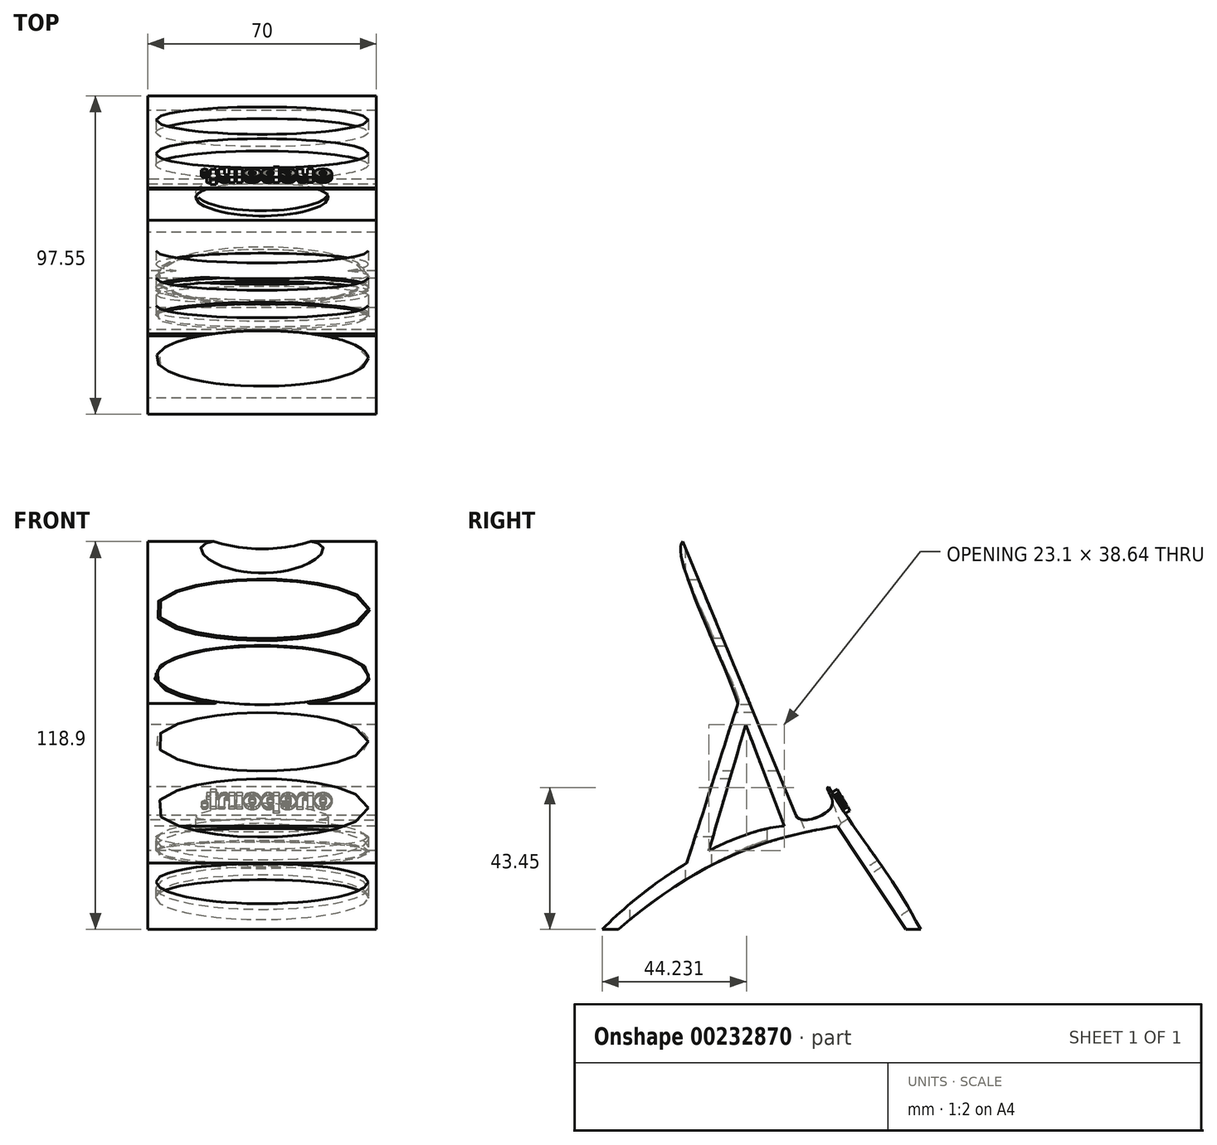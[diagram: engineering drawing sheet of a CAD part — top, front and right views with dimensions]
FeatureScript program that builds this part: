
annotation { "Feature Type Name" : "Feature", "Feature Type Description" : "" }
export const myFeature = defineFeature(function(context is Context, id is Id, definition is map)
    precondition{}
    {
        {
            var Q0;
            Q0=qCreatedBy(makeId("Right.planeOp"),FACE);
            var sketch = newSketch(context, id + "F0", { "sketchPlane" : qUnion([Q0])});
            skFitSpline(sketch, "E0", {"points": [v(42.97, 20.37) * mm, v(14.77, 64.07) * mm], "startDerivative": vector(-33.57, 62.35) * mm, "endDerivative": vector(-38.78, 64) * mm});
            skLineSegment(sketch, "E1", {"start": v(-29.92, 139.27) * mm, "end": v(4.83, 55.39) * mm});
            skFitSpline(sketch, "E2", {"points": [v(4.83, 55.39) * mm, v(15.94, 58.63) * mm, v(14.77, 64.07) * mm], "startDerivative": vector(5.7, -17.02) * mm, "endDerivative": vector(10.42, 3.26) * mm});
            skLineSegment(sketch, "E3", {"start": v(17.48, 52.06) * mm, "end": v(38.5, 20.37) * mm});
            skLineSegment(sketch, "E4", {"start": v(-10.58, 83.14) * mm, "end": v(1.2, 52.06) * mm});
            skFitSpline(sketch, "E5", {"points": [v(-29.92, 139.27) * mm, v(-12.97, 89.66) * mm], "startDerivative": vector(-12.17, -12.55) * mm, "endDerivative": vector(13.11, -40.92) * mm});
            skFitSpline(sketch, "E6", {"points": [v(1.2, 52.06) * mm, v(-54.58, 20.37) * mm], "startDerivative": vector(-40.28, -2.72) * mm, "endDerivative": vector(-57.87, -57.98) * mm});
            skFitSpline(sketch, "E7", {"points": [v(17.48, 52.06) * mm, v(-49.6, 20.37) * mm], "startDerivative": vector(-52.44, -9.28) * mm, "endDerivative": vector(-83.1, -72.38) * mm});
            skLineSegment(sketch, "E8", {"start": v(-49.6, 20.37) * mm, "end": v(-54.58, 20.37) * mm});
            skLineSegment(sketch, "E9", {"start": v(42.97, 20.37) * mm, "end": v(38.5, 20.37) * mm});
            skLineSegment(sketch, "E10", {"start": v(38.5, 20.37) * mm, "end": v(-49.6, 20.37) * mm});
            skFitSpline(sketch, "E11", {"points": [v(-10.58, 83.14) * mm, v(-21.9, 44.5) * mm], "startDerivative": vector(-11.4, -38.7) * mm, "endDerivative": vector(-11.4, -38.7) * mm});
            skFitSpline(sketch, "E12", {"points": [v(-12.97, 89.66) * mm, v(-28.67, 40.72) * mm], "startDerivative": vector(-16.26, -49.82) * mm, "endDerivative": vector(-16.26, -49.82) * mm});
            skSolve(sketch);
        }
        {
            var Q0;
            Q0=makeQuery(id+"F0.imprint","IMPRINT",FACE,{"disambiguationData":[TD([[makeQuery(id+"F0.imprint","IMPRINT",EDGE,{"derivedFrom":sQuery(id+"F0.wireOp",EDGE,"e2dd9e04-bce8-43ee-a2f2-a46b7d135692")}),-1.0]])]});
            var Q1;
            Q1=makeQuery(id+"F0.imprint","IMPRINT",FACE,{"disambiguationData":[TD([[makeQuery(id+"F0.imprint","IMPRINT",EDGE,{"derivedFrom":sQuery(id+"F0.wireOp",EDGE,"dd02e322-1caa-4adf-9807-8f987be65d11")}),1.0]])]});
            var Q2;
            Q2=makeQuery(id+"F0.imprint","IMPRINT",FACE,{"disambiguationData":[TD([[makeQuery(id+"F0.imprint","IMPRINT",EDGE,{"derivedFrom":sQuery(id+"F0.wireOp",EDGE,"E0")}),1.0]])]});
            var Q3;
            {var subQ0=sQuery(id+"F0.wireOp",EDGE,"E6");Q3=makeQuery(id+"F0.imprint","IMPRINT",FACE,{"disambiguationData":[TD([[makeQuery(id+"F0.imprint","IMPRINT",EDGE,{"derivedFrom":subQ0}),1.0]])]});}
            extrude(context, id + "F1", {"entities" : qUnion([Q0, Q1, Q2, Q3]), "depth" : 70 * mm});
        }
        {
            var Q0;
            Q0=makeQuery(id+"F1.opExtrude","SWEPT_FACE",FACE,{"disambiguationData":[OSD([sQuery(id+"F0.wireOp",EDGE,"E3")])]});
            var sketch = newSketch(context, id + "F2", { "sketchPlane" : qUnion([Q0])});
            skEllipse(sketch, "E13", {"center": v(35, 25.97) * mm, "majorRadius": 32.5 * mm, "minorRadius": 7.82 * mm, "majorAxis": v(1, 0)});
            skEllipse(sketch, "E14.0.1.0", {"center": v(35, 7.97) * mm, "majorRadius": 32.5 * mm, "minorRadius": 7.82 * mm, "majorAxis": v(1, 0)});
            skLineSegment(sketch, "E14.direction1", {"start": v(35, 25.97) * mm, "end": v(57.03, 25.97) * mm, "construction": true});
            skLineSegment(sketch, "E14.direction2", {"start": v(35, 25.97) * mm, "end": v(35, 7.97) * mm, "construction": true});
            skSolve(sketch);
        }
        {
            var Q0;
            Q0=qSketchRegion(id+"F2",true);
            var Q1;
            Q1=makeQuery(id+"F1.opExtrude","SWEPT_FACE",FACE,{"disambiguationData":[OSD([sQuery(id+"F0.wireOp",EDGE,"E0")])]});
            extrude(context, id + "F3", {"entities" : qUnion([Q0]), "operationType" : NewBodyOperationType.REMOVE, "endBound" : BoundingType.UP_TO_SURFACE, "oppositeDirection" : true, "endBoundEntityFace" : qUnion([Q1]), "depth" : 25 * mm});
        }
        {
            var Q0;
            Q0=qCreatedBy(makeId("Top.planeOp"),FACE);
            var sketch = newSketch(context, id + "F4", { "sketchPlane" : qUnion([Q0])});
            skEllipse(sketch, "E15", {"center": v(35, -37.48) * mm, "majorRadius": 32.5 * mm, "minorRadius": 8.5 * mm, "majorAxis": v(1, 0)});
            skEllipse(sketch, "E16.0.1.0", {"center": v(35, -12.48) * mm, "majorRadius": 32.5 * mm, "minorRadius": 8.5 * mm, "majorAxis": v(1, 0)});
            skLineSegment(sketch, "E16.direction1", {"start": v(35, -37.48) * mm, "end": v(60, -37.48) * mm, "construction": true});
            skLineSegment(sketch, "E16.direction2", {"start": v(35, -37.48) * mm, "end": v(35, -12.48) * mm, "construction": true});
            skSolve(sketch);
        }
        {
            var Q0;
            Q0=makeQuery(id+"F4.imprint","IMPRINT",FACE,{"disambiguationData":[TD([[makeQuery(id+"F4.imprint","IMPRINT",EDGE,{"derivedFrom":sQuery(id+"F4.wireOp",EDGE,"E16.0.1.0")}),1.0]])]});
            var Q1;
            Q1=makeQuery(id+"F4.imprint","IMPRINT",FACE,{"disambiguationData":[TD([[makeQuery(id+"F4.imprint","IMPRINT",EDGE,{"derivedFrom":sQuery(id+"F4.wireOp",EDGE,"E16.0.2.0")}),1.0]])]});
            var Q2;
            Q2=makeQuery(id+"F1.opExtrude","SWEPT_FACE",FACE,{"disambiguationData":[OSD([sQuery(id+"F0.wireOp",EDGE,"E6")])]});
            extrude(context, id + "F5", {"entities" : qUnion([Q0, Q1]), "operationType" : NewBodyOperationType.REMOVE, "endBound" : BoundingType.UP_TO_SURFACE, "endBoundEntityFace" : qUnion([Q2]), "depth" : 25 * mm});
        }
        {
            var Q0;
            Q0=qCreatedBy(makeId("Front.planeOp"),FACE);
            cPlane(context, id + "F6", {"entities" : qUnion([Q0]), "cplaneType" : CPlaneType.OFFSET, "offset" : 70 * mm, "width" : 150 * mm, "height" : 150 * mm});
        }
        {
            var Q0;
            Q0=qCreatedBy(id+"F6.planeOp",FACE);
            var sketch = newSketch(context, id + "F7", { "sketchPlane" : qUnion([Q0])});
            skEllipse(sketch, "E17", {"center": v(35, 118.52) * mm, "majorRadius": 32.5 * mm, "minorRadius": 8.93 * mm, "majorAxis": v(1, 0)});
            skEllipse(sketch, "E18.0.1.0", {"center": v(35, 98.22) * mm, "majorRadius": 32.5 * mm, "minorRadius": 8.93 * mm, "majorAxis": v(1, 0)});
            skEllipse(sketch, "E18.0.2.0", {"center": v(35, 77.92) * mm, "majorRadius": 32.5 * mm, "minorRadius": 8.93 * mm, "majorAxis": v(1, 0)});
            skEllipse(sketch, "E18.0.3.0", {"center": v(35, 57.62) * mm, "majorRadius": 32.5 * mm, "minorRadius": 8.93 * mm, "majorAxis": v(1, 0)});
            skEllipse(sketch, "E18.0.4.0", {"center": v(35, 37.32) * mm, "majorRadius": 32.5 * mm, "minorRadius": 8.93 * mm, "majorAxis": v(1, 0)});
            skEllipse(sketch, "E18.0.5.0", {"center": v(35, 17.02) * mm, "majorRadius": 32.5 * mm, "minorRadius": 8.93 * mm, "majorAxis": v(1, 0)});
            skLineSegment(sketch, "E18.direction1", {"start": v(35, 118.52) * mm, "end": v(60, 118.52) * mm, "construction": true});
            skLineSegment(sketch, "E18.direction2", {"start": v(35, 118.52) * mm, "end": v(35, 98.22) * mm, "construction": true});
            skSolve(sketch);
        }
        {
            var Q0;
            Q0=makeQuery(id+"F7.imprint","IMPRINT",FACE,{"disambiguationData":[TD([[makeQuery(id+"F7.imprint","IMPRINT",EDGE,{"derivedFrom":sQuery(id+"F7.wireOp",EDGE,"E18.0.3.0")}),1.0]])]});
            var Q1;
            Q1=makeQuery(id+"F1.opExtrude","SWEPT_FACE",FACE,{"disambiguationData":[OSD([sQuery(id+"F0.wireOp",EDGE,"E11")])]});
            extrude(context, id + "F8", {"entities" : qUnion([Q0]), "operationType" : NewBodyOperationType.REMOVE, "endBound" : BoundingType.UP_TO_SURFACE, "oppositeDirection" : true, "endBoundEntityFace" : qUnion([Q1]), "depth" : 25 * mm});
        }
        {
            var Q0;
            Q0=makeQuery(id+"F7.imprint","IMPRINT",FACE,{"disambiguationData":[TD([[makeQuery(id+"F7.imprint","IMPRINT",EDGE,{"derivedFrom":sQuery(id+"F7.wireOp",EDGE,"E17")}),1.0]])]});
            var Q1;
            Q1=makeQuery(id+"F7.imprint","IMPRINT",FACE,{"disambiguationData":[TD([[makeQuery(id+"F7.imprint","IMPRINT",EDGE,{"derivedFrom":sQuery(id+"F7.wireOp",EDGE,"E18.0.1.0")}),1.0]])]});
            var Q2;
            Q2=makeQuery(id+"F7.imprint","IMPRINT",FACE,{"disambiguationData":[TD([[makeQuery(id+"F7.imprint","IMPRINT",EDGE,{"derivedFrom":sQuery(id+"F7.wireOp",EDGE,"E18.0.2.0")}),1.0]])]});
            var Q3;
            Q3=makeQuery(id+"F1.opExtrude","SWEPT_FACE",FACE,{"disambiguationData":[OSD([sQuery(id+"F0.wireOp",EDGE,"E1")])]});
            extrude(context, id + "F9", {"entities" : qUnion([Q0, Q1, Q2]), "operationType" : NewBodyOperationType.REMOVE, "endBound" : BoundingType.UP_TO_SURFACE, "oppositeDirection" : true, "endBoundEntityFace" : qUnion([Q3]), "depth" : 25 * mm});
        }
        {
            var Q0;
            Q0=makeQuery(id+"F1.opExtrude","SWEPT_FACE",FACE,{"disambiguationData":[OSD([sQuery(id+"F0.wireOp",EDGE,"E1")])]});
            var Q1;
            Q1=makeQuery(id+"F1.opExtrude","SWEPT_EDGE",EDGE,{"disambiguationData":[OSD([sQuery(id+"F0.wireOp",EDGE,"E1"),sQuery(id+"F0.wireOp",EDGE,"E5")])]});
            cPlane(context, id + "F10", {"entities" : qUnion([Q0, Q1]), "cplaneType" : CPlaneType.LINE_ANGLE, "offset" : 25 * mm, "angle" : 90 * degree, "width" : 150 * mm, "height" : 150 * mm});
        }
        {
            var Q0;
            Q0=qCreatedBy(id+"F10.planeOp",FACE);
            var sketch = newSketch(context, id + "F11", { "sketchPlane" : qUnion([Q0])});
            skEllipse(sketch, "E19", {"center": v(35, 31.9) * mm, "majorRadius": 20.28 * mm, "minorRadius": 5.5 * mm, "majorAxis": v(-1, 0)});
            skSolve(sketch);
        }
        {
            var Q0;
            Q0=qSketchRegion(id+"F11",true);
            var Q1;
            Q1=makeQuery(id+"F1.opExtrude","SWEPT_FACE",FACE,{"disambiguationData":[OSD([sQuery(id+"F0.wireOp",EDGE,"E7")])]});
            extrude(context, id + "F12", {"entities" : qUnion([Q0]), "operationType" : NewBodyOperationType.REMOVE, "endBound" : BoundingType.THROUGH_ALL, "oppositeDirection" : true, "endBoundEntityFace" : qUnion([Q1]), "depth" : 25 * mm});
        }
        {
            var Q0;
            Q0=makeQuery(id+"F3.boolean.opBoolean","COPY",EDGE,{"derivedFrom":makeQuery(id+"F3.opExtrude","TWEAK_EDGE",EDGE,{"derivedFrom":[makeQuery(id+"F1.opExtrude","SWEPT_FACE",FACE,{"disambiguationData":[OSD([sQuery(id+"F0.wireOp",EDGE,"E0")])]}),makeQuery(id+"F2.imprint","IMPRINT",EDGE,{"derivedFrom":sQuery(id+"F2.wireOp",EDGE,"E13")})]})});
            var Q1;
            Q1=makeQuery(id+"F3.boolean.opBoolean","COPY",EDGE,{"derivedFrom":makeQuery(id+"F3.opExtrude","TWEAK_EDGE",EDGE,{"derivedFrom":[makeQuery(id+"F1.opExtrude","SWEPT_FACE",FACE,{"disambiguationData":[OSD([sQuery(id+"F0.wireOp",EDGE,"E0")])]}),makeQuery(id+"F2.imprint","IMPRINT",EDGE,{"derivedFrom":sQuery(id+"F2.wireOp",EDGE,"E14.0.1.0")})]})});
            var Q2;
            Q2=makeQuery(id+"F3.boolean.opBoolean","COPY",EDGE,{"derivedFrom":makeQuery(id+"F3.opExtrude","TWEAK_EDGE",EDGE,{"derivedFrom":[makeQuery(id+"F1.opExtrude","SWEPT_FACE",FACE,{"disambiguationData":[OSD([sQuery(id+"F0.wireOp",EDGE,"E0")])]}),makeQuery(id+"F2.imprint","IMPRINT",EDGE,{"derivedFrom":sQuery(id+"F2.wireOp",EDGE,"E14.0.2.0")})]})});
            var Q3;
            Q3=makeQuery(id+"F3.boolean.opBoolean","COPY",EDGE,{"derivedFrom":makeQuery(id+"F3.opExtrude","CAP_EDGE",EDGE,{"disambiguationData":[OSD([sQuery(id+"F2.wireOp",EDGE,"E13")])],"isStart":true})});
            var Q4;
            Q4=makeQuery(id+"F3.boolean.opBoolean","COPY",EDGE,{"derivedFrom":makeQuery(id+"F3.opExtrude","CAP_EDGE",EDGE,{"disambiguationData":[OSD([sQuery(id+"F2.wireOp",EDGE,"E14.0.1.0")])],"isStart":true})});
            var Q5;
            Q5=makeQuery(id+"F3.boolean.opBoolean","COPY",EDGE,{"derivedFrom":makeQuery(id+"F3.opExtrude","CAP_EDGE",EDGE,{"disambiguationData":[OSD([sQuery(id+"F2.wireOp",EDGE,"E14.0.2.0")])],"isStart":true})});
            var Q6;
            Q6=makeQuery(id+"F8.boolean.opBoolean","INTERSECT",EDGE,{"derivedFrom":[makeQuery(id+"F1.opExtrude","SWEPT_FACE",FACE,{"disambiguationData":[OSD([sQuery(id+"F0.wireOp",EDGE,"61fd75d5-24df-4c68-a095-90f6d82b9ead")])]}),makeQuery(id+"F8.opExtrude","SWEPT_FACE",FACE,{"disambiguationData":[OSD([sQuery(id+"F7.wireOp",EDGE,"E18.0.3.0")])]})]});
            var Q7;
            Q7=makeQuery(id+"F8.boolean.opBoolean","COPY",EDGE,{"derivedFrom":makeQuery(id+"F8.opExtrude","CAP_EDGE",EDGE,{"disambiguationData":[OSD([sQuery(id+"F7.wireOp",EDGE,"E18.0.3.0")])],"isStart":false})});
            var Q8;
            Q8=makeQuery(id+"F8.boolean.opBoolean","INTERSECT",EDGE,{"derivedFrom":[makeQuery(id+"F1.opExtrude","SWEPT_FACE",FACE,{"disambiguationData":[OSD([sQuery(id+"F0.wireOp",EDGE,"61fd75d5-24df-4c68-a095-90f6d82b9ead")])]}),makeQuery(id+"F8.opExtrude","SWEPT_FACE",FACE,{"disambiguationData":[OSD([sQuery(id+"F7.wireOp",EDGE,"E18.0.4.0")])]})]});
            var Q9;
            {var subQ0=sQuery(id+"F0.wireOp",EDGE,"5998eb2a-c125-4484-9ba4-89ed062cae3a");var subQ1=sQuery(id+"F0.wireOp",EDGE,"E7");var subQ2=sQuery(id+"F7.wireOp",EDGE,"E18.0.4.0");Q9=makeQuery(id+"F8.boolean.opBoolean","COPY",EDGE,{"disambiguationData":[TD([makeQuery(id+"F1.opExtrude","SWEPT_FACE",FACE,{"disambiguationData":[OSD([subQ0]),TDD([makeQuery(id+"F0.imprint","IMPRINT",EDGE,{"disambiguationData":[TD([[makeQuery(id+"F0.imprint","INTERSECT",VERTEX,{"derivedFrom":[subQ0,sQuery(id+"F0.wireOp",EDGE,"umK4nLRB-749r-FOEl-6r3i-m92kNIwFStfI")]}),-1.0]])],"derivedFrom":subQ0})])]}),makeQuery(id+"F1.opExtrude","SWEPT_FACE",FACE,{"disambiguationData":[OSD([subQ1])]}),makeQuery(id+"F8.opExtrude","SWEPT_FACE",FACE,{"disambiguationData":[OSD([subQ2])]}),makeQuery(id+"F8.opExtrude","CAP_FACE",FACE,{"disambiguationData":[OSD([subQ2])],"isStart":false})])],"derivedFrom":makeQuery(id+"F8.opExtrude","CAP_EDGE",EDGE,{"disambiguationData":[OSD([subQ2])],"isStart":false})});}
            var Q10;
            Q10=makeQuery(id+"F8.boolean.opBoolean","INTERSECT",EDGE,{"derivedFrom":[makeQuery(id+"F1.opExtrude","SWEPT_FACE",FACE,{"disambiguationData":[OSD([sQuery(id+"F0.wireOp",EDGE,"61fd75d5-24df-4c68-a095-90f6d82b9ead")])]}),makeQuery(id+"F8.opExtrude","SWEPT_FACE",FACE,{"disambiguationData":[OSD([sQuery(id+"F7.wireOp",EDGE,"E18.0.5.0")])]})]});
            var Q11;
            Q11=makeQuery(id+"F8.boolean.opBoolean","COPY",EDGE,{"derivedFrom":makeQuery(id+"F8.opExtrude","CAP_EDGE",EDGE,{"disambiguationData":[OSD([sQuery(id+"F7.wireOp",EDGE,"E18.0.5.0")])],"isStart":false})});
            var Q12;
            {var subQ0=sQuery(id+"F0.wireOp",EDGE,"5998eb2a-c125-4484-9ba4-89ed062cae3a");Q12=makeQuery(id+"F9.boolean.opBoolean","INTERSECT",EDGE,{"derivedFrom":[makeQuery(id+"F1.opExtrude","SWEPT_FACE",FACE,{"disambiguationData":[OSD([subQ0]),TDD([makeQuery(id+"F0.imprint","IMPRINT",EDGE,{"disambiguationData":[TD([[makeQuery(id+"F0.imprint","INTERSECT",VERTEX,{"derivedFrom":[subQ0,sQuery(id+"F0.wireOp",EDGE,"E4")]}),1.0]])],"derivedFrom":subQ0})])]}),makeQuery(id+"F9.opExtrude","SWEPT_FACE",FACE,{"disambiguationData":[OSD([sQuery(id+"F7.wireOp",EDGE,"E18.0.2.0")])]})]});}
            var Q13;
            Q13=makeQuery(id+"F9.boolean.opBoolean","INTERSECT",EDGE,{"derivedFrom":[makeQuery(id+"F1.opExtrude","SWEPT_FACE",FACE,{"disambiguationData":[OSD([sQuery(id+"F0.wireOp",EDGE,"61fd75d5-24df-4c68-a095-90f6d82b9ead")])]}),makeQuery(id+"F9.opExtrude","SWEPT_FACE",FACE,{"disambiguationData":[OSD([sQuery(id+"F7.wireOp",EDGE,"E18.0.2.0")])]})]});
            var Q14;
            Q14=makeQuery(id+"F5.boolean.opBoolean","COPY",EDGE,{"derivedFrom":makeQuery(id+"F5.opExtrude","TWEAK_EDGE",EDGE,{"derivedFrom":[makeQuery(id+"F1.opExtrude","SWEPT_FACE",FACE,{"disambiguationData":[OSD([sQuery(id+"F0.wireOp",EDGE,"E6")])]}),makeQuery(id+"F4.imprint","IMPRINT",EDGE,{"derivedFrom":sQuery(id+"F4.wireOp",EDGE,"E16.0.1.0")})]})});
            var Q15;
            Q15=makeQuery(id+"F5.boolean.opBoolean","INTERSECT",EDGE,{"derivedFrom":[makeQuery(id+"F1.opExtrude","SWEPT_FACE",FACE,{"disambiguationData":[OSD([sQuery(id+"F0.wireOp",EDGE,"E7")])]}),makeQuery(id+"F5.opExtrude","SWEPT_FACE",FACE,{"disambiguationData":[OSD([sQuery(id+"F4.wireOp",EDGE,"E16.0.1.0")])]})]});
            var Q16;
            Q16=makeQuery(id+"F5.boolean.opBoolean","INTERSECT",EDGE,{"derivedFrom":[makeQuery(id+"F1.opExtrude","SWEPT_FACE",FACE,{"disambiguationData":[OSD([sQuery(id+"F0.wireOp",EDGE,"E7")])]}),makeQuery(id+"F5.opExtrude","SWEPT_FACE",FACE,{"disambiguationData":[OSD([sQuery(id+"F4.wireOp",EDGE,"E15")])]})]});
            var Q17;
            Q17=makeQuery(id+"F5.boolean.opBoolean","COPY",EDGE,{"derivedFrom":makeQuery(id+"F5.opExtrude","TWEAK_EDGE",EDGE,{"derivedFrom":[makeQuery(id+"F1.opExtrude","SWEPT_FACE",FACE,{"disambiguationData":[OSD([sQuery(id+"F0.wireOp",EDGE,"E6")])]}),makeQuery(id+"F4.imprint","IMPRINT",EDGE,{"derivedFrom":sQuery(id+"F4.wireOp",EDGE,"E15")})]})});
            var Q18;
            Q18=makeQuery(id+"F9.boolean.opBoolean","COPY",EDGE,{"derivedFrom":makeQuery(id+"F9.opExtrude","TWEAK_EDGE",EDGE,{"derivedFrom":[makeQuery(id+"F1.opExtrude","SWEPT_FACE",FACE,{"disambiguationData":[OSD([sQuery(id+"F0.wireOp",EDGE,"E1")])]}),makeQuery(id+"F7.imprint","IMPRINT",EDGE,{"derivedFrom":sQuery(id+"F7.wireOp",EDGE,"E18.0.2.0")})]})});
            var Q19;
            Q19=makeQuery(id+"F9.boolean.opBoolean","COPY",EDGE,{"derivedFrom":makeQuery(id+"F9.opExtrude","TWEAK_EDGE",EDGE,{"derivedFrom":[makeQuery(id+"F1.opExtrude","SWEPT_FACE",FACE,{"disambiguationData":[OSD([sQuery(id+"F0.wireOp",EDGE,"E1")])]}),makeQuery(id+"F7.imprint","IMPRINT",EDGE,{"derivedFrom":sQuery(id+"F7.wireOp",EDGE,"E18.0.1.0")})]})});
            var Q20;
            Q20=makeQuery(id+"F9.boolean.opBoolean","INTERSECT",EDGE,{"derivedFrom":[makeQuery(id+"F1.opExtrude","SWEPT_FACE",FACE,{"disambiguationData":[OSD([sQuery(id+"F0.wireOp",EDGE,"E5")])]}),makeQuery(id+"F9.opExtrude","SWEPT_FACE",FACE,{"disambiguationData":[OSD([sQuery(id+"F7.wireOp",EDGE,"E18.0.1.0")])]})]});
            var Q21;
            Q21=makeQuery(id+"F9.boolean.opBoolean","INTERSECT",EDGE,{"derivedFrom":[makeQuery(id+"F1.opExtrude","SWEPT_FACE",FACE,{"disambiguationData":[OSD([sQuery(id+"F0.wireOp",EDGE,"E5")])]}),makeQuery(id+"F9.opExtrude","SWEPT_FACE",FACE,{"disambiguationData":[OSD([sQuery(id+"F7.wireOp",EDGE,"E17")])]})]});
            var Q22;
            Q22=makeQuery(id+"F9.boolean.opBoolean","COPY",EDGE,{"derivedFrom":makeQuery(id+"F9.opExtrude","TWEAK_EDGE",EDGE,{"derivedFrom":[makeQuery(id+"F1.opExtrude","SWEPT_FACE",FACE,{"disambiguationData":[OSD([sQuery(id+"F0.wireOp",EDGE,"E1")])]}),makeQuery(id+"F7.imprint","IMPRINT",EDGE,{"derivedFrom":sQuery(id+"F7.wireOp",EDGE,"E17")})]})});
            fillet(context, id + "F13", {"entities" : qUnion([Q0, Q1, Q2, Q3, Q4, Q5, Q6, Q7, Q8, Q9, Q10, Q11, Q12, Q13, Q14, Q15, Q16, Q17, Q18, Q19, Q20, Q21, Q22]), "radius" : 0.5 * mm, "tangentPropagation" : true, "allowEdgeOverflow" : false});
        }
        {
            var Q0;
            Q0=makeQuery(id+"F1.opExtrude","SWEPT_EDGE",EDGE,{"disambiguationData":[OSD([sQuery(id+"F0.wireOp",EDGE,"E0"),sQuery(id+"F0.wireOp",EDGE,"E2")])]});
            cPlane(context, id + "F14", {"entities" : qUnion([Q0]), "cplaneType" : CPlaneType.LINE_ANGLE, "offset" : 25 * mm, "angle" : 150 * degree, "width" : 150 * mm, "height" : 150 * mm});
        }
        {
            var Q0;
            Q0=qCreatedBy(id+"F14.planeOp",FACE);
            var sketch = newSketch(context, id + "F15", { "sketchPlane" : qUnion([Q0])});
            skLineSegment(sketch, "E20", {"start": v(-54.12, 39.93) * mm, "end": v(-54.9, 40.17) * mm});
            skLineSegment(sketch, "E21", {"start": v(-54.9, 40.17) * mm, "end": v(-55.54, 40.6) * mm});
            skLineSegment(sketch, "E22", {"start": v(-55.54, 40.6) * mm, "end": v(-56.02, 41.2) * mm});
            skLineSegment(sketch, "E23", {"start": v(-56.02, 41.2) * mm, "end": v(-56.3, 41.94) * mm});
            skLineSegment(sketch, "E24", {"start": v(-56.3, 41.94) * mm, "end": v(-56.33, 42.13) * mm});
            skLineSegment(sketch, "E25", {"start": v(-56.33, 42.13) * mm, "end": v(-56.34, 42.37) * mm});
            skLineSegment(sketch, "E26", {"start": v(-56.34, 42.62) * mm, "end": v(-56.32, 42.83) * mm});
            skLineSegment(sketch, "E27", {"start": v(-56.32, 42.83) * mm, "end": v(-56.06, 43.6) * mm});
            skLineSegment(sketch, "E28", {"start": v(-56.06, 43.6) * mm, "end": v(-55.56, 44.26) * mm});
            skLineSegment(sketch, "E29", {"start": v(-55.56, 44.26) * mm, "end": v(-55.18, 44.57) * mm});
            skLineSegment(sketch, "E30", {"start": v(-55.18, 44.57) * mm, "end": v(-54.75, 44.8) * mm});
            skLineSegment(sketch, "E31", {"start": v(-54.75, 44.8) * mm, "end": v(-54.28, 44.94) * mm});
            skLineSegment(sketch, "E32", {"start": v(-54.28, 44.94) * mm, "end": v(-53.77, 45) * mm});
            skLineSegment(sketch, "E33", {"start": v(-53.77, 45) * mm, "end": v(-53.19, 44.98) * mm});
            skLineSegment(sketch, "E34", {"start": v(-53.19, 44.98) * mm, "end": v(-52.64, 44.84) * mm});
            skLineSegment(sketch, "E35", {"start": v(-52.64, 44.84) * mm, "end": v(-52.15, 44.6) * mm});
            skLineSegment(sketch, "E36", {"start": v(-52.15, 44.6) * mm, "end": v(-51.7, 44.26) * mm});
            skLineSegment(sketch, "E37", {"start": v(-51.7, 44.26) * mm, "end": v(-51.23, 43.63) * mm});
            skLineSegment(sketch, "E38", {"start": v(-51.23, 43.63) * mm, "end": v(-50.98, 42.9) * mm});
            skLineSegment(sketch, "E39", {"start": v(-50.98, 42.9) * mm, "end": v(-50.95, 42.7) * mm});
            skLineSegment(sketch, "E40", {"start": v(-50.95, 42.7) * mm, "end": v(-50.95, 42.45) * mm});
            skLineSegment(sketch, "E41", {"start": v(-50.95, 42.45) * mm, "end": v(-50.96, 42.2) * mm});
            skLineSegment(sketch, "E42", {"start": v(-50.96, 42.2) * mm, "end": v(-50.99, 42) * mm});
            skLineSegment(sketch, "E43", {"start": v(-50.99, 42) * mm, "end": v(-51.26, 41.25) * mm});
            skLineSegment(sketch, "E44", {"start": v(-51.26, 41.25) * mm, "end": v(-51.73, 40.64) * mm});
            skLineSegment(sketch, "E45", {"start": v(-51.73, 40.64) * mm, "end": v(-52.37, 40.19) * mm});
            skLineSegment(sketch, "E46", {"start": v(-52.37, 40.19) * mm, "end": v(-53.14, 39.94) * mm});
            skLineSegment(sketch, "E47", {"start": v(-53.14, 39.94) * mm, "end": v(-53.63, 39.9) * mm});
            skLineSegment(sketch, "E48", {"start": v(-53.63, 39.9) * mm, "end": v(-54.12, 39.93) * mm});
            skLineSegment(sketch, "E49", {"start": v(-54.12, 39.93) * mm, "end": v(-54.12, 39.93) * mm});
            skLineSegment(sketch, "E50", {"start": v(-53.38, 41.4) * mm, "end": v(-53.15, 41.5) * mm});
            skLineSegment(sketch, "E51", {"start": v(-53.15, 41.5) * mm, "end": v(-52.96, 41.63) * mm});
            skLineSegment(sketch, "E52", {"start": v(-52.96, 41.63) * mm, "end": v(-52.8, 41.82) * mm});
            skLineSegment(sketch, "E53", {"start": v(-52.8, 41.82) * mm, "end": v(-52.7, 42.06) * mm});
            skLineSegment(sketch, "E54", {"start": v(-52.7, 42.06) * mm, "end": v(-52.63, 42.42) * mm});
            skLineSegment(sketch, "E55", {"start": v(-52.63, 42.42) * mm, "end": v(-52.67, 42.77) * mm});
            skLineSegment(sketch, "E56", {"start": v(-52.67, 42.77) * mm, "end": v(-52.8, 43.04) * mm});
            skLineSegment(sketch, "E57", {"start": v(-52.8, 43.04) * mm, "end": v(-52.97, 43.26) * mm});
            skLineSegment(sketch, "E58", {"start": v(-52.97, 43.26) * mm, "end": v(-53.2, 43.42) * mm});
            skLineSegment(sketch, "E59", {"start": v(-53.2, 43.42) * mm, "end": v(-53.46, 43.52) * mm});
            skLineSegment(sketch, "E60", {"start": v(-53.46, 43.52) * mm, "end": v(-53.57, 43.54) * mm});
            skLineSegment(sketch, "E61", {"start": v(-53.57, 43.54) * mm, "end": v(-53.66, 43.55) * mm});
            skLineSegment(sketch, "E62", {"start": v(-53.66, 43.55) * mm, "end": v(-53.88, 43.52) * mm});
            skLineSegment(sketch, "E63", {"start": v(-53.88, 43.52) * mm, "end": v(-54.1, 43.44) * mm});
            skLineSegment(sketch, "E64", {"start": v(-54.1, 43.44) * mm, "end": v(-54.28, 43.32) * mm});
            skLineSegment(sketch, "E65", {"start": v(-54.28, 43.32) * mm, "end": v(-54.43, 43.16) * mm});
            skLineSegment(sketch, "E66", {"start": v(-54.43, 43.16) * mm, "end": v(-54.55, 42.97) * mm});
            skLineSegment(sketch, "E67", {"start": v(-54.55, 42.97) * mm, "end": v(-54.62, 42.76) * mm});
            skLineSegment(sketch, "E68", {"start": v(-54.62, 42.76) * mm, "end": v(-54.65, 42.62) * mm});
            skLineSegment(sketch, "E69", {"start": v(-54.65, 42.62) * mm, "end": v(-54.66, 42.46) * mm});
            skLineSegment(sketch, "E70", {"start": v(-54.66, 42.46) * mm, "end": v(-54.65, 42.3) * mm});
            skLineSegment(sketch, "E71", {"start": v(-54.65, 42.3) * mm, "end": v(-54.62, 42.18) * mm});
            skLineSegment(sketch, "E72", {"start": v(-54.62, 42.18) * mm, "end": v(-54.52, 41.9) * mm});
            skLineSegment(sketch, "E73", {"start": v(-54.52, 41.9) * mm, "end": v(-54.35, 41.68) * mm});
            skLineSegment(sketch, "E74", {"start": v(-54.35, 41.68) * mm, "end": v(-54.14, 41.5) * mm});
            skLineSegment(sketch, "E75", {"start": v(-54.14, 41.5) * mm, "end": v(-53.89, 41.4) * mm});
            skLineSegment(sketch, "E76", {"start": v(-53.89, 41.4) * mm, "end": v(-53.64, 41.37) * mm});
            skLineSegment(sketch, "E77", {"start": v(-53.64, 41.37) * mm, "end": v(-53.38, 41.4) * mm});
            skLineSegment(sketch, "E78", {"start": v(-53.38, 41.4) * mm, "end": v(-53.38, 41.4) * mm});
            skLineSegment(sketch, "E79", {"start": v(-50.6, 42.43) * mm, "end": v(-50.6, 44.87) * mm});
            skLineSegment(sketch, "E80", {"start": v(-50.6, 44.87) * mm, "end": v(-48.87, 44.87) * mm});
            skLineSegment(sketch, "E81", {"start": v(-48.87, 44.87) * mm, "end": v(-48.87, 44.24) * mm});
            skLineSegment(sketch, "E82", {"start": v(-48.87, 44.24) * mm, "end": v(-48.68, 44.42) * mm});
            skLineSegment(sketch, "E83", {"start": v(-48.68, 44.42) * mm, "end": v(-48.43, 44.66) * mm});
            skLineSegment(sketch, "E84", {"start": v(-48.43, 44.66) * mm, "end": v(-48.16, 44.81) * mm});
            skLineSegment(sketch, "E85", {"start": v(-48.16, 44.81) * mm, "end": v(-47.8, 44.94) * mm});
            skLineSegment(sketch, "E86", {"start": v(-47.8, 44.94) * mm, "end": v(-47.4, 44.99) * mm});
            skLineSegment(sketch, "E87", {"start": v(-47.4, 44.99) * mm, "end": v(-47.01, 44.95) * mm});
            skLineSegment(sketch, "E88", {"start": v(-47.01, 44.95) * mm, "end": v(-46.64, 44.83) * mm});
            skLineSegment(sketch, "E89", {"start": v(-46.64, 44.83) * mm, "end": v(-46.33, 44.63) * mm});
            skLineSegment(sketch, "E90", {"start": v(-46.33, 44.63) * mm, "end": v(-46.1, 44.38) * mm});
            skLineSegment(sketch, "E91", {"start": v(-46.1, 44.38) * mm, "end": v(-45.92, 44.06) * mm});
            skLineSegment(sketch, "E92", {"start": v(-45.92, 44.06) * mm, "end": v(-45.8, 43.66) * mm});
            skLineSegment(sketch, "E93", {"start": v(-45.8, 43.66) * mm, "end": v(-45.78, 43.6) * mm});
            skLineSegment(sketch, "E94", {"start": v(-45.78, 43.6) * mm, "end": v(-45.77, 43.52) * mm});
            skLineSegment(sketch, "E95", {"start": v(-45.77, 43.52) * mm, "end": v(-45.77, 43.4) * mm});
            skLineSegment(sketch, "E96", {"start": v(-45.77, 43.4) * mm, "end": v(-45.76, 43.24) * mm});
            skLineSegment(sketch, "E97", {"start": v(-45.76, 43.24) * mm, "end": v(-45.76, 43) * mm});
            skLineSegment(sketch, "E98", {"start": v(-45.76, 43) * mm, "end": v(-45.76, 42.69) * mm});
            skLineSegment(sketch, "E99", {"start": v(-45.76, 42.69) * mm, "end": v(-45.75, 42.27) * mm});
            skLineSegment(sketch, "E100", {"start": v(-45.75, 42.27) * mm, "end": v(-45.75, 41.75) * mm});
            skLineSegment(sketch, "E101", {"start": v(-45.75, 41.75) * mm, "end": v(-45.75, 39.99) * mm});
            skLineSegment(sketch, "E102", {"start": v(-45.75, 39.99) * mm, "end": v(-47.48, 39.99) * mm});
            skLineSegment(sketch, "E103", {"start": v(-47.48, 39.99) * mm, "end": v(-47.48, 41.4) * mm});
            skLineSegment(sketch, "E104", {"start": v(-47.48, 41.4) * mm, "end": v(-47.48, 41.88) * mm});
            skLineSegment(sketch, "E105", {"start": v(-47.48, 41.88) * mm, "end": v(-47.49, 42.23) * mm});
            skLineSegment(sketch, "E106", {"start": v(-47.49, 42.23) * mm, "end": v(-47.5, 42.49) * mm});
            skLineSegment(sketch, "E107", {"start": v(-47.5, 42.49) * mm, "end": v(-47.5, 42.67) * mm});
            skLineSegment(sketch, "E108", {"start": v(-47.5, 42.67) * mm, "end": v(-47.5, 42.79) * mm});
            skLineSegment(sketch, "E109", {"start": v(-47.5, 42.79) * mm, "end": v(-47.5, 42.87) * mm});
            skLineSegment(sketch, "E110", {"start": v(-47.5, 42.87) * mm, "end": v(-47.52, 42.92) * mm});
            skLineSegment(sketch, "E111", {"start": v(-47.52, 42.92) * mm, "end": v(-47.53, 42.96) * mm});
            skLineSegment(sketch, "E112", {"start": v(-47.53, 42.96) * mm, "end": v(-47.62, 43.15) * mm});
            skLineSegment(sketch, "E113", {"start": v(-47.62, 43.15) * mm, "end": v(-47.74, 43.3) * mm});
            skLineSegment(sketch, "E114", {"start": v(-47.74, 43.3) * mm, "end": v(-47.9, 43.4) * mm});
            skLineSegment(sketch, "E115", {"start": v(-47.9, 43.4) * mm, "end": v(-48.1, 43.44) * mm});
            skLineSegment(sketch, "E116", {"start": v(-48.1, 43.44) * mm, "end": v(-48.33, 43.42) * mm});
            skLineSegment(sketch, "E117", {"start": v(-48.33, 43.42) * mm, "end": v(-48.53, 43.34) * mm});
            skLineSegment(sketch, "E118", {"start": v(-48.53, 43.34) * mm, "end": v(-48.7, 43.19) * mm});
            skLineSegment(sketch, "E119", {"start": v(-48.7, 43.19) * mm, "end": v(-48.82, 42.98) * mm});
            skLineSegment(sketch, "E120", {"start": v(-48.82, 42.98) * mm, "end": v(-48.83, 42.94) * mm});
            skLineSegment(sketch, "E121", {"start": v(-48.83, 42.94) * mm, "end": v(-48.84, 42.9) * mm});
            skLineSegment(sketch, "E122", {"start": v(-48.84, 42.9) * mm, "end": v(-48.85, 42.82) * mm});
            skLineSegment(sketch, "E123", {"start": v(-48.85, 42.82) * mm, "end": v(-48.85, 42.7) * mm});
            skLineSegment(sketch, "E124", {"start": v(-48.85, 42.7) * mm, "end": v(-48.86, 42.52) * mm});
            skLineSegment(sketch, "E125", {"start": v(-48.86, 42.52) * mm, "end": v(-48.86, 42.26) * mm});
            skLineSegment(sketch, "E126", {"start": v(-48.86, 42.26) * mm, "end": v(-48.86, 41.9) * mm});
            skLineSegment(sketch, "E127", {"start": v(-48.86, 41.9) * mm, "end": v(-48.87, 41.43) * mm});
            skLineSegment(sketch, "E128", {"start": v(-48.87, 41.43) * mm, "end": v(-48.87, 39.99) * mm});
            skLineSegment(sketch, "E129", {"start": v(-48.87, 39.99) * mm, "end": v(-50.6, 39.99) * mm});
            skLineSegment(sketch, "E130", {"start": v(-50.6, 39.99) * mm, "end": v(-50.6, 42.43) * mm});
            skLineSegment(sketch, "E131", {"start": v(-50.6, 42.43) * mm, "end": v(-50.6, 42.43) * mm});
            skLineSegment(sketch, "E132", {"start": v(-43.28, 39.9) * mm, "end": v(-44.1, 40.15) * mm});
            skLineSegment(sketch, "E133", {"start": v(-44.1, 40.15) * mm, "end": v(-44.75, 40.62) * mm});
            skLineSegment(sketch, "E134", {"start": v(-44.75, 40.62) * mm, "end": v(-45.17, 41.17) * mm});
            skLineSegment(sketch, "E135", {"start": v(-45.17, 41.17) * mm, "end": v(-45.4, 41.84) * mm});
            skLineSegment(sketch, "E136", {"start": v(-45.4, 41.84) * mm, "end": v(-45.43, 41.96) * mm});
            skLineSegment(sketch, "E137", {"start": v(-45.43, 41.96) * mm, "end": v(-45.44, 42.07) * mm});
            skLineSegment(sketch, "E138", {"start": v(-45.44, 42.07) * mm, "end": v(-45.45, 42.22) * mm});
            skLineSegment(sketch, "E139", {"start": v(-45.45, 42.22) * mm, "end": v(-45.45, 42.42) * mm});
            skLineSegment(sketch, "E140", {"start": v(-45.45, 42.42) * mm, "end": v(-45.45, 42.63) * mm});
            skLineSegment(sketch, "E141", {"start": v(-45.45, 42.63) * mm, "end": v(-45.44, 42.77) * mm});
            skLineSegment(sketch, "E142", {"start": v(-45.44, 42.77) * mm, "end": v(-45.43, 42.88) * mm});
            skLineSegment(sketch, "E143", {"start": v(-45.43, 42.88) * mm, "end": v(-45.4, 43) * mm});
            skLineSegment(sketch, "E144", {"start": v(-45.4, 43) * mm, "end": v(-45.15, 43.7) * mm});
            skLineSegment(sketch, "E145", {"start": v(-45.15, 43.7) * mm, "end": v(-44.72, 44.29) * mm});
            skLineSegment(sketch, "E146", {"start": v(-44.72, 44.29) * mm, "end": v(-44.15, 44.71) * mm});
            skLineSegment(sketch, "E147", {"start": v(-44.15, 44.71) * mm, "end": v(-43.47, 44.95) * mm});
            skLineSegment(sketch, "E148", {"start": v(-43.47, 44.95) * mm, "end": v(-43.24, 44.98) * mm});
            skLineSegment(sketch, "E149", {"start": v(-43.24, 44.98) * mm, "end": v(-42.95, 44.98) * mm});
            skLineSegment(sketch, "E150", {"start": v(-42.95, 44.98) * mm, "end": v(-42.66, 44.97) * mm});
            skLineSegment(sketch, "E151", {"start": v(-42.66, 44.97) * mm, "end": v(-42.42, 44.94) * mm});
            skLineSegment(sketch, "E152", {"start": v(-42.42, 44.94) * mm, "end": v(-41.75, 44.7) * mm});
            skLineSegment(sketch, "E153", {"start": v(-41.75, 44.7) * mm, "end": v(-41.22, 44.3) * mm});
            skLineSegment(sketch, "E154", {"start": v(-41.22, 44.3) * mm, "end": v(-40.83, 43.74) * mm});
            skLineSegment(sketch, "E155", {"start": v(-40.83, 43.74) * mm, "end": v(-40.59, 43.03) * mm});
            skLineSegment(sketch, "E156", {"start": v(-40.59, 43.03) * mm, "end": v(-40.56, 42.8) * mm});
            skLineSegment(sketch, "E157", {"start": v(-40.56, 42.8) * mm, "end": v(-40.53, 42.54) * mm});
            skLineSegment(sketch, "E158", {"start": v(-40.53, 42.54) * mm, "end": v(-40.52, 42.29) * mm});
            skLineSegment(sketch, "E159", {"start": v(-40.52, 42.29) * mm, "end": v(-40.52, 42.1) * mm});
            skLineSegment(sketch, "E160", {"start": v(-40.52, 42.1) * mm, "end": v(-40.54, 41.95) * mm});
            skLineSegment(sketch, "E161", {"start": v(-40.54, 41.95) * mm, "end": v(-43.79, 41.95) * mm});
            skLineSegment(sketch, "E162", {"start": v(-43.79, 41.95) * mm, "end": v(-43.78, 41.9) * mm});
            skLineSegment(sketch, "E163", {"start": v(-43.78, 41.9) * mm, "end": v(-43.75, 41.83) * mm});
            skLineSegment(sketch, "E164", {"start": v(-43.75, 41.83) * mm, "end": v(-43.7, 41.73) * mm});
            skLineSegment(sketch, "E165", {"start": v(-43.7, 41.73) * mm, "end": v(-43.6, 41.55) * mm});
            skLineSegment(sketch, "E166", {"start": v(-43.6, 41.55) * mm, "end": v(-43.44, 41.4) * mm});
            skLineSegment(sketch, "E167", {"start": v(-43.44, 41.4) * mm, "end": v(-43.25, 41.28) * mm});
            skLineSegment(sketch, "E168", {"start": v(-43.25, 41.28) * mm, "end": v(-43.04, 41.2) * mm});
            skLineSegment(sketch, "E169", {"start": v(-43.04, 41.2) * mm, "end": v(-42.87, 41.18) * mm});
            skLineSegment(sketch, "E170", {"start": v(-42.87, 41.18) * mm, "end": v(-42.68, 41.18) * mm});
            skLineSegment(sketch, "E171", {"start": v(-42.68, 41.18) * mm, "end": v(-42.48, 41.2) * mm});
            skLineSegment(sketch, "E172", {"start": v(-42.48, 41.2) * mm, "end": v(-42.32, 41.24) * mm});
            skLineSegment(sketch, "E173", {"start": v(-42.32, 41.24) * mm, "end": v(-42.06, 41.37) * mm});
            skLineSegment(sketch, "E174", {"start": v(-42.06, 41.37) * mm, "end": v(-41.8, 41.56) * mm});
            skLineSegment(sketch, "E175", {"start": v(-41.8, 41.56) * mm, "end": v(-41.67, 41.67) * mm});
            skLineSegment(sketch, "E176", {"start": v(-41.67, 41.67) * mm, "end": v(-41.18, 41.27) * mm});
            skLineSegment(sketch, "E177", {"start": v(-41.18, 41.27) * mm, "end": v(-40.7, 40.87) * mm});
            skLineSegment(sketch, "E178", {"start": v(-40.7, 40.87) * mm, "end": v(-40.8, 40.77) * mm});
            skLineSegment(sketch, "E179", {"start": v(-40.8, 40.77) * mm, "end": v(-41.4, 40.25) * mm});
            skLineSegment(sketch, "E180", {"start": v(-41.4, 40.25) * mm, "end": v(-42.17, 39.94) * mm});
            skLineSegment(sketch, "E181", {"start": v(-42.17, 39.94) * mm, "end": v(-42.29, 39.92) * mm});
            skLineSegment(sketch, "E182", {"start": v(-42.29, 39.92) * mm, "end": v(-42.4, 39.9) * mm});
            skLineSegment(sketch, "E183", {"start": v(-42.4, 39.9) * mm, "end": v(-42.56, 39.9) * mm});
            skLineSegment(sketch, "E184", {"start": v(-42.56, 39.9) * mm, "end": v(-42.78, 39.9) * mm});
            skLineSegment(sketch, "E185", {"start": v(-42.78, 39.9) * mm, "end": v(-42.94, 39.9) * mm});
            skLineSegment(sketch, "E186", {"start": v(-42.94, 39.9) * mm, "end": v(-43.1, 39.9) * mm});
            skLineSegment(sketch, "E187", {"start": v(-43.1, 39.9) * mm, "end": v(-43.2, 39.9) * mm});
            skLineSegment(sketch, "E188", {"start": v(-43.2, 39.9) * mm, "end": v(-43.28, 39.9) * mm});
            skLineSegment(sketch, "E189", {"start": v(-43.28, 39.9) * mm, "end": v(-43.28, 39.9) * mm});
            skLineSegment(sketch, "E190", {"start": v(-42.15, 42.88) * mm, "end": v(-42.16, 42.95) * mm});
            skLineSegment(sketch, "E191", {"start": v(-42.16, 42.95) * mm, "end": v(-42.2, 43.05) * mm});
            skLineSegment(sketch, "E192", {"start": v(-42.2, 43.05) * mm, "end": v(-42.23, 43.17) * mm});
            skLineSegment(sketch, "E193", {"start": v(-42.23, 43.17) * mm, "end": v(-42.27, 43.27) * mm});
            skLineSegment(sketch, "E194", {"start": v(-42.27, 43.27) * mm, "end": v(-42.42, 43.48) * mm});
            skLineSegment(sketch, "E195", {"start": v(-42.42, 43.48) * mm, "end": v(-42.62, 43.63) * mm});
            skLineSegment(sketch, "E196", {"start": v(-42.62, 43.63) * mm, "end": v(-42.86, 43.7) * mm});
            skLineSegment(sketch, "E197", {"start": v(-42.86, 43.7) * mm, "end": v(-43.11, 43.7) * mm});
            skLineSegment(sketch, "E198", {"start": v(-43.11, 43.7) * mm, "end": v(-43.34, 43.62) * mm});
            skLineSegment(sketch, "E199", {"start": v(-43.34, 43.62) * mm, "end": v(-43.53, 43.47) * mm});
            skLineSegment(sketch, "E200", {"start": v(-43.53, 43.47) * mm, "end": v(-43.68, 43.26) * mm});
            skLineSegment(sketch, "E201", {"start": v(-43.68, 43.26) * mm, "end": v(-43.79, 43) * mm});
            skLineSegment(sketch, "E202", {"start": v(-43.79, 43) * mm, "end": v(-43.82, 42.85) * mm});
            skLineSegment(sketch, "E203", {"start": v(-43.82, 42.85) * mm, "end": v(-42.99, 42.85) * mm});
            skLineSegment(sketch, "E204", {"start": v(-42.99, 42.85) * mm, "end": v(-42.73, 42.85) * mm});
            skLineSegment(sketch, "E205", {"start": v(-42.73, 42.85) * mm, "end": v(-42.54, 42.85) * mm});
            skLineSegment(sketch, "E206", {"start": v(-42.54, 42.85) * mm, "end": v(-42.39, 42.86) * mm});
            skLineSegment(sketch, "E207", {"start": v(-42.39, 42.86) * mm, "end": v(-42.28, 42.86) * mm});
            skLineSegment(sketch, "E208", {"start": v(-42.28, 42.86) * mm, "end": v(-42.21, 42.86) * mm});
            skLineSegment(sketch, "E209", {"start": v(-42.21, 42.86) * mm, "end": v(-42.17, 42.86) * mm});
            skLineSegment(sketch, "E210", {"start": v(-42.17, 42.86) * mm, "end": v(-42.15, 42.87) * mm});
            skLineSegment(sketch, "E211", {"start": v(-42.15, 42.87) * mm, "end": v(-42.15, 42.88) * mm});
            skLineSegment(sketch, "E212", {"start": v(-42.15, 42.88) * mm, "end": v(-42.15, 42.88) * mm});
            skLineSegment(sketch, "E213", {"start": v(-40.19, 41.72) * mm, "end": v(-40.19, 44.88) * mm});
            skLineSegment(sketch, "E214", {"start": v(-40.19, 44.88) * mm, "end": v(-38.46, 44.88) * mm});
            skLineSegment(sketch, "E215", {"start": v(-38.46, 44.88) * mm, "end": v(-38.46, 44.25) * mm});
            skLineSegment(sketch, "E216", {"start": v(-38.46, 44.25) * mm, "end": v(-38.3, 44.42) * mm});
            skLineSegment(sketch, "E217", {"start": v(-38.3, 44.42) * mm, "end": v(-38.02, 44.66) * mm});
            skLineSegment(sketch, "E218", {"start": v(-38.02, 44.66) * mm, "end": v(-37.74, 44.83) * mm});
            skLineSegment(sketch, "E219", {"start": v(-37.74, 44.83) * mm, "end": v(-37.43, 44.94) * mm});
            skLineSegment(sketch, "E220", {"start": v(-37.43, 44.94) * mm, "end": v(-37.08, 44.99) * mm});
            skLineSegment(sketch, "E221", {"start": v(-37.08, 44.99) * mm, "end": v(-36.37, 44.9) * mm});
            skLineSegment(sketch, "E222", {"start": v(-36.37, 44.9) * mm, "end": v(-35.75, 44.57) * mm});
            skLineSegment(sketch, "E223", {"start": v(-35.75, 44.57) * mm, "end": v(-35.26, 44.04) * mm});
            skLineSegment(sketch, "E224", {"start": v(-35.26, 44.04) * mm, "end": v(-34.94, 43.35) * mm});
            skLineSegment(sketch, "E225", {"start": v(-34.94, 43.35) * mm, "end": v(-34.82, 42.57) * mm});
            skLineSegment(sketch, "E226", {"start": v(-34.82, 42.57) * mm, "end": v(-34.88, 41.76) * mm});
            skLineSegment(sketch, "E227", {"start": v(-34.88, 41.76) * mm, "end": v(-35.1, 41.12) * mm});
            skLineSegment(sketch, "E228", {"start": v(-35.1, 41.12) * mm, "end": v(-35.44, 40.6) * mm});
            skLineSegment(sketch, "E229", {"start": v(-35.44, 40.6) * mm, "end": v(-35.91, 40.19) * mm});
            skLineSegment(sketch, "E230", {"start": v(-35.91, 40.19) * mm, "end": v(-36.47, 39.94) * mm});
            skLineSegment(sketch, "E231", {"start": v(-36.47, 39.94) * mm, "end": v(-36.59, 39.92) * mm});
            skLineSegment(sketch, "E232", {"start": v(-36.59, 39.92) * mm, "end": v(-36.69, 39.9) * mm});
            skLineSegment(sketch, "E233", {"start": v(-36.69, 39.9) * mm, "end": v(-36.8, 39.9) * mm});
            skLineSegment(sketch, "E234", {"start": v(-36.8, 39.9) * mm, "end": v(-36.98, 39.9) * mm});
            skLineSegment(sketch, "E235", {"start": v(-36.98, 39.9) * mm, "end": v(-37.16, 39.9) * mm});
            skLineSegment(sketch, "E236", {"start": v(-37.16, 39.9) * mm, "end": v(-37.28, 39.9) * mm});
            skLineSegment(sketch, "E237", {"start": v(-37.28, 39.9) * mm, "end": v(-37.38, 39.92) * mm});
            skLineSegment(sketch, "E238", {"start": v(-37.38, 39.92) * mm, "end": v(-37.48, 39.94) * mm});
            skLineSegment(sketch, "E239", {"start": v(-37.48, 39.94) * mm, "end": v(-37.71, 40.02) * mm});
            skLineSegment(sketch, "E240", {"start": v(-37.71, 40.02) * mm, "end": v(-37.92, 40.12) * mm});
            skLineSegment(sketch, "E241", {"start": v(-37.92, 40.12) * mm, "end": v(-38.12, 40.26) * mm});
            skLineSegment(sketch, "E242", {"start": v(-38.12, 40.26) * mm, "end": v(-38.32, 40.43) * mm});
            skLineSegment(sketch, "E243", {"start": v(-38.32, 40.43) * mm, "end": v(-38.46, 40.56) * mm});
            skLineSegment(sketch, "E244", {"start": v(-38.46, 40.56) * mm, "end": v(-38.46, 38.54) * mm});
            skLineSegment(sketch, "E245", {"start": v(-38.46, 38.54) * mm, "end": v(-40.19, 38.54) * mm});
            skLineSegment(sketch, "E246", {"start": v(-40.19, 38.54) * mm, "end": v(-40.19, 41.72) * mm});
            skLineSegment(sketch, "E247", {"start": v(-40.19, 41.72) * mm, "end": v(-40.19, 41.72) * mm});
            skLineSegment(sketch, "E248", {"start": v(-37.34, 41.35) * mm, "end": v(-37.15, 41.4) * mm});
            skLineSegment(sketch, "E249", {"start": v(-37.15, 41.4) * mm, "end": v(-36.95, 41.52) * mm});
            skLineSegment(sketch, "E250", {"start": v(-36.95, 41.52) * mm, "end": v(-36.79, 41.67) * mm});
            skLineSegment(sketch, "E251", {"start": v(-36.79, 41.67) * mm, "end": v(-36.66, 41.84) * mm});
            skLineSegment(sketch, "E252", {"start": v(-36.66, 41.84) * mm, "end": v(-36.57, 42.06) * mm});
            skLineSegment(sketch, "E253", {"start": v(-36.57, 42.06) * mm, "end": v(-36.53, 42.3) * mm});
            skLineSegment(sketch, "E254", {"start": v(-36.53, 42.3) * mm, "end": v(-36.53, 42.53) * mm});
            skLineSegment(sketch, "E255", {"start": v(-36.53, 42.53) * mm, "end": v(-36.57, 42.76) * mm});
            skLineSegment(sketch, "E256", {"start": v(-36.57, 42.76) * mm, "end": v(-36.72, 43.1) * mm});
            skLineSegment(sketch, "E257", {"start": v(-36.72, 43.1) * mm, "end": v(-36.97, 43.37) * mm});
            skLineSegment(sketch, "E258", {"start": v(-36.97, 43.37) * mm, "end": v(-37.28, 43.51) * mm});
            skLineSegment(sketch, "E259", {"start": v(-37.28, 43.51) * mm, "end": v(-37.64, 43.53) * mm});
            skLineSegment(sketch, "E260", {"start": v(-37.64, 43.53) * mm, "end": v(-37.91, 43.44) * mm});
            skLineSegment(sketch, "E261", {"start": v(-37.91, 43.44) * mm, "end": v(-38.15, 43.27) * mm});
            skLineSegment(sketch, "E262", {"start": v(-38.15, 43.27) * mm, "end": v(-38.33, 43.04) * mm});
            skLineSegment(sketch, "E263", {"start": v(-38.33, 43.04) * mm, "end": v(-38.45, 42.75) * mm});
            skLineSegment(sketch, "E264", {"start": v(-38.45, 42.75) * mm, "end": v(-38.47, 42.61) * mm});
            skLineSegment(sketch, "E265", {"start": v(-38.47, 42.61) * mm, "end": v(-38.48, 42.44) * mm});
            skLineSegment(sketch, "E266", {"start": v(-38.48, 42.44) * mm, "end": v(-38.47, 42.27) * mm});
            skLineSegment(sketch, "E267", {"start": v(-38.47, 42.27) * mm, "end": v(-38.45, 42.13) * mm});
            skLineSegment(sketch, "E268", {"start": v(-38.45, 42.13) * mm, "end": v(-38.34, 41.85) * mm});
            skLineSegment(sketch, "E269", {"start": v(-38.34, 41.85) * mm, "end": v(-38.17, 41.62) * mm});
            skLineSegment(sketch, "E270", {"start": v(-38.17, 41.62) * mm, "end": v(-37.95, 41.45) * mm});
            skLineSegment(sketch, "E271", {"start": v(-37.95, 41.45) * mm, "end": v(-37.7, 41.35) * mm});
            skLineSegment(sketch, "E272", {"start": v(-37.7, 41.35) * mm, "end": v(-37.53, 41.33) * mm});
            skLineSegment(sketch, "E273", {"start": v(-37.53, 41.33) * mm, "end": v(-37.34, 41.35) * mm});
            skLineSegment(sketch, "E274", {"start": v(-28.9, 42.44) * mm, "end": v(-28.9, 44.88) * mm});
            skLineSegment(sketch, "E275", {"start": v(-28.9, 44.88) * mm, "end": v(-27.16, 44.88) * mm});
            skLineSegment(sketch, "E276", {"start": v(-27.16, 44.88) * mm, "end": v(-27.16, 40) * mm});
            skLineSegment(sketch, "E277", {"start": v(-27.16, 40) * mm, "end": v(-28.9, 40) * mm});
            skLineSegment(sketch, "E278", {"start": v(-28.9, 40) * mm, "end": v(-28.9, 42.44) * mm});
            skLineSegment(sketch, "E279", {"start": v(-32.41, 39.93) * mm, "end": v(-33.2, 40.17) * mm});
            skLineSegment(sketch, "E280", {"start": v(-33.2, 40.17) * mm, "end": v(-33.84, 40.6) * mm});
            skLineSegment(sketch, "E281", {"start": v(-33.84, 40.6) * mm, "end": v(-34.31, 41.2) * mm});
            skLineSegment(sketch, "E282", {"start": v(-34.31, 41.2) * mm, "end": v(-34.6, 41.94) * mm});
            skLineSegment(sketch, "E283", {"start": v(-34.6, 41.94) * mm, "end": v(-34.63, 42.13) * mm});
            skLineSegment(sketch, "E284", {"start": v(-34.63, 42.13) * mm, "end": v(-34.64, 42.37) * mm});
            skLineSegment(sketch, "E285", {"start": v(-34.64, 42.37) * mm, "end": v(-34.64, 42.62) * mm});
            skLineSegment(sketch, "E286", {"start": v(-34.65, 42.42) * mm, "end": v(-34.64, 42.62) * mm});
            skLineSegment(sketch, "E287", {"start": v(-34.62, 42.83) * mm, "end": v(-34.36, 43.6) * mm});
            skLineSegment(sketch, "E288", {"start": v(-34.36, 43.6) * mm, "end": v(-33.86, 44.26) * mm});
            skLineSegment(sketch, "E289", {"start": v(-33.86, 44.26) * mm, "end": v(-33.48, 44.57) * mm});
            skLineSegment(sketch, "E290", {"start": v(-33.48, 44.57) * mm, "end": v(-33.05, 44.8) * mm});
            skLineSegment(sketch, "E291", {"start": v(-33.05, 44.8) * mm, "end": v(-32.58, 44.94) * mm});
            skLineSegment(sketch, "E292", {"start": v(-32.58, 44.94) * mm, "end": v(-32.07, 45) * mm});
            skLineSegment(sketch, "E293", {"start": v(-32.07, 45) * mm, "end": v(-31.49, 44.98) * mm});
            skLineSegment(sketch, "E294", {"start": v(-31.49, 44.98) * mm, "end": v(-30.94, 44.84) * mm});
            skLineSegment(sketch, "E295", {"start": v(-30.94, 44.84) * mm, "end": v(-30.44, 44.6) * mm});
            skLineSegment(sketch, "E296", {"start": v(-30.44, 44.6) * mm, "end": v(-30, 44.26) * mm});
            skLineSegment(sketch, "E297", {"start": v(-30, 44.26) * mm, "end": v(-29.53, 43.63) * mm});
            skLineSegment(sketch, "E298", {"start": v(-29.53, 43.63) * mm, "end": v(-29.27, 42.9) * mm});
            skLineSegment(sketch, "E299", {"start": v(-29.27, 42.9) * mm, "end": v(-29.25, 42.7) * mm});
            skLineSegment(sketch, "E300", {"start": v(-29.25, 42.7) * mm, "end": v(-29.24, 42.45) * mm});
            skLineSegment(sketch, "E301", {"start": v(-29.24, 42.45) * mm, "end": v(-29.26, 42.2) * mm});
            skLineSegment(sketch, "E302", {"start": v(-29.26, 42.2) * mm, "end": v(-29.29, 42) * mm});
            skLineSegment(sketch, "E303", {"start": v(-29.29, 42) * mm, "end": v(-29.55, 41.25) * mm});
            skLineSegment(sketch, "E304", {"start": v(-29.55, 41.25) * mm, "end": v(-30.03, 40.64) * mm});
            skLineSegment(sketch, "E305", {"start": v(-30.03, 40.64) * mm, "end": v(-30.67, 40.19) * mm});
            skLineSegment(sketch, "E306", {"start": v(-30.67, 40.19) * mm, "end": v(-31.44, 39.94) * mm});
            skLineSegment(sketch, "E307", {"start": v(-31.44, 39.94) * mm, "end": v(-31.93, 39.9) * mm});
            skLineSegment(sketch, "E308", {"start": v(-31.93, 39.9) * mm, "end": v(-32.41, 39.93) * mm});
            skLineSegment(sketch, "E309", {"start": v(-31.68, 41.4) * mm, "end": v(-31.45, 41.5) * mm});
            skLineSegment(sketch, "E310", {"start": v(-31.45, 41.5) * mm, "end": v(-31.26, 41.63) * mm});
            skLineSegment(sketch, "E311", {"start": v(-31.26, 41.63) * mm, "end": v(-31.1, 41.82) * mm});
            skLineSegment(sketch, "E312", {"start": v(-31.1, 41.82) * mm, "end": v(-31, 42.06) * mm});
            skLineSegment(sketch, "E313", {"start": v(-31, 42.06) * mm, "end": v(-30.93, 42.42) * mm});
            skLineSegment(sketch, "E314", {"start": v(-30.93, 42.42) * mm, "end": v(-30.97, 42.77) * mm});
            skLineSegment(sketch, "E315", {"start": v(-30.97, 42.77) * mm, "end": v(-31.1, 43.04) * mm});
            skLineSegment(sketch, "E316", {"start": v(-31.1, 43.04) * mm, "end": v(-31.27, 43.26) * mm});
            skLineSegment(sketch, "E317", {"start": v(-31.27, 43.26) * mm, "end": v(-31.5, 43.42) * mm});
            skLineSegment(sketch, "E318", {"start": v(-31.5, 43.42) * mm, "end": v(-31.76, 43.52) * mm});
            skLineSegment(sketch, "E319", {"start": v(-31.76, 43.52) * mm, "end": v(-31.87, 43.54) * mm});
            skLineSegment(sketch, "E320", {"start": v(-31.87, 43.54) * mm, "end": v(-31.96, 43.55) * mm});
            skLineSegment(sketch, "E321", {"start": v(-31.96, 43.55) * mm, "end": v(-32.18, 43.52) * mm});
            skLineSegment(sketch, "E322", {"start": v(-32.18, 43.52) * mm, "end": v(-32.4, 43.44) * mm});
            skLineSegment(sketch, "E323", {"start": v(-32.4, 43.44) * mm, "end": v(-32.58, 43.32) * mm});
            skLineSegment(sketch, "E324", {"start": v(-32.58, 43.32) * mm, "end": v(-32.73, 43.16) * mm});
            skLineSegment(sketch, "E325", {"start": v(-32.73, 43.16) * mm, "end": v(-32.85, 42.97) * mm});
            skLineSegment(sketch, "E326", {"start": v(-32.85, 42.97) * mm, "end": v(-32.92, 42.76) * mm});
            skLineSegment(sketch, "E327", {"start": v(-32.92, 42.76) * mm, "end": v(-32.95, 42.62) * mm});
            skLineSegment(sketch, "E328", {"start": v(-32.95, 42.62) * mm, "end": v(-32.95, 42.46) * mm});
            skLineSegment(sketch, "E329", {"start": v(-32.95, 42.46) * mm, "end": v(-32.95, 42.3) * mm});
            skLineSegment(sketch, "E330", {"start": v(-32.95, 42.3) * mm, "end": v(-32.92, 42.18) * mm});
            skLineSegment(sketch, "E331", {"start": v(-32.92, 42.18) * mm, "end": v(-32.82, 41.9) * mm});
            skLineSegment(sketch, "E332", {"start": v(-32.82, 41.9) * mm, "end": v(-32.65, 41.68) * mm});
            skLineSegment(sketch, "E333", {"start": v(-32.65, 41.68) * mm, "end": v(-32.44, 41.5) * mm});
            skLineSegment(sketch, "E334", {"start": v(-32.44, 41.5) * mm, "end": v(-32.19, 41.4) * mm});
            skLineSegment(sketch, "E335", {"start": v(-32.19, 41.4) * mm, "end": v(-31.94, 41.37) * mm});
            skLineSegment(sketch, "E336", {"start": v(-31.94, 41.37) * mm, "end": v(-31.68, 41.4) * mm});
            skLineSegment(sketch, "E337", {"start": v(-31.68, 41.4) * mm, "end": v(-31.68, 41.4) * mm});
            skLineSegment(sketch, "E338", {"start": v(-26.6, 42.44) * mm, "end": v(-26.6, 44.88) * mm});
            skLineSegment(sketch, "E339", {"start": v(-26.6, 44.88) * mm, "end": v(-24.86, 44.88) * mm});
            skLineSegment(sketch, "E340", {"start": v(-24.86, 44.88) * mm, "end": v(-24.86, 44.23) * mm});
            skLineSegment(sketch, "E341", {"start": v(-24.86, 44.23) * mm, "end": v(-24.68, 44.41) * mm});
            skLineSegment(sketch, "E342", {"start": v(-24.68, 44.41) * mm, "end": v(-24.33, 44.71) * mm});
            skLineSegment(sketch, "E343", {"start": v(-24.33, 44.71) * mm, "end": v(-23.96, 44.9) * mm});
            skLineSegment(sketch, "E344", {"start": v(-23.96, 44.9) * mm, "end": v(-23.55, 45) * mm});
            skLineSegment(sketch, "E345", {"start": v(-23.55, 45) * mm, "end": v(-23.12, 44.97) * mm});
            skLineSegment(sketch, "E346", {"start": v(-23.12, 44.97) * mm, "end": v(-22.6, 44.82) * mm});
            skLineSegment(sketch, "E347", {"start": v(-22.6, 44.82) * mm, "end": v(-22.2, 44.52) * mm});
            skLineSegment(sketch, "E348", {"start": v(-22.2, 44.52) * mm, "end": v(-21.91, 44.08) * mm});
            skLineSegment(sketch, "E349", {"start": v(-21.91, 44.08) * mm, "end": v(-21.76, 43.53) * mm});
            skLineSegment(sketch, "E350", {"start": v(-21.76, 43.53) * mm, "end": v(-21.76, 43.35) * mm});
            skLineSegment(sketch, "E351", {"start": v(-21.76, 43.35) * mm, "end": v(-21.75, 42.95) * mm});
            skLineSegment(sketch, "E352", {"start": v(-21.75, 42.95) * mm, "end": v(-21.74, 42.39) * mm});
            skLineSegment(sketch, "E353", {"start": v(-21.74, 42.39) * mm, "end": v(-21.74, 41.7) * mm});
            skLineSegment(sketch, "E354", {"start": v(-21.74, 41.7) * mm, "end": v(-21.74, 40) * mm});
            skLineSegment(sketch, "E355", {"start": v(-21.74, 40) * mm, "end": v(-23.47, 40) * mm});
            skLineSegment(sketch, "E356", {"start": v(-23.47, 40) * mm, "end": v(-23.47, 41.39) * mm});
            skLineSegment(sketch, "E357", {"start": v(-23.47, 41.39) * mm, "end": v(-23.47, 41.89) * mm});
            skLineSegment(sketch, "E358", {"start": v(-23.47, 41.89) * mm, "end": v(-23.47, 42.27) * mm});
            skLineSegment(sketch, "E359", {"start": v(-23.47, 42.27) * mm, "end": v(-23.48, 42.55) * mm});
            skLineSegment(sketch, "E360", {"start": v(-23.48, 42.55) * mm, "end": v(-23.49, 42.75) * mm});
            skLineSegment(sketch, "E361", {"start": v(-23.49, 42.75) * mm, "end": v(-23.5, 42.89) * mm});
            skLineSegment(sketch, "E362", {"start": v(-23.5, 42.89) * mm, "end": v(-23.52, 42.98) * mm});
            skLineSegment(sketch, "E363", {"start": v(-23.52, 42.98) * mm, "end": v(-23.54, 43.05) * mm});
            skLineSegment(sketch, "E364", {"start": v(-23.54, 43.05) * mm, "end": v(-23.58, 43.12) * mm});
            skLineSegment(sketch, "E365", {"start": v(-23.58, 43.12) * mm, "end": v(-23.73, 43.31) * mm});
            skLineSegment(sketch, "E366", {"start": v(-23.73, 43.31) * mm, "end": v(-23.95, 43.43) * mm});
            skLineSegment(sketch, "E367", {"start": v(-23.95, 43.43) * mm, "end": v(-24.2, 43.46) * mm});
            skLineSegment(sketch, "E368", {"start": v(-24.2, 43.46) * mm, "end": v(-24.45, 43.4) * mm});
            skLineSegment(sketch, "E369", {"start": v(-24.45, 43.4) * mm, "end": v(-24.63, 43.26) * mm});
            skLineSegment(sketch, "E370", {"start": v(-24.63, 43.26) * mm, "end": v(-24.77, 43.07) * mm});
            skLineSegment(sketch, "E371", {"start": v(-24.77, 43.07) * mm, "end": v(-24.8, 43) * mm});
            skLineSegment(sketch, "E372", {"start": v(-24.8, 43) * mm, "end": v(-24.82, 42.93) * mm});
            skLineSegment(sketch, "E373", {"start": v(-24.82, 42.93) * mm, "end": v(-24.84, 42.83) * mm});
            skLineSegment(sketch, "E374", {"start": v(-24.84, 42.83) * mm, "end": v(-24.85, 42.7) * mm});
            skLineSegment(sketch, "E375", {"start": v(-24.85, 42.7) * mm, "end": v(-24.86, 42.5) * mm});
            skLineSegment(sketch, "E376", {"start": v(-24.86, 42.5) * mm, "end": v(-24.86, 42.22) * mm});
            skLineSegment(sketch, "E377", {"start": v(-24.86, 42.22) * mm, "end": v(-24.86, 41.85) * mm});
            skLineSegment(sketch, "E378", {"start": v(-24.86, 41.85) * mm, "end": v(-24.86, 41.36) * mm});
            skLineSegment(sketch, "E379", {"start": v(-24.86, 41.36) * mm, "end": v(-24.86, 40) * mm});
            skLineSegment(sketch, "E380", {"start": v(-24.86, 40) * mm, "end": v(-26.6, 40) * mm});
            skLineSegment(sketch, "E381", {"start": v(-26.6, 40) * mm, "end": v(-26.6, 42.44) * mm});
            skLineSegment(sketch, "E382", {"start": v(-26.6, 42.44) * mm, "end": v(-26.6, 42.44) * mm});
            skLineSegment(sketch, "E383", {"start": v(-20.9, 41.78) * mm, "end": v(-20.9, 43.53) * mm});
            skLineSegment(sketch, "E384", {"start": v(-20.9, 43.53) * mm, "end": v(-21.49, 43.53) * mm});
            skLineSegment(sketch, "E385", {"start": v(-21.49, 43.53) * mm, "end": v(-21.49, 44.92) * mm});
            skLineSegment(sketch, "E386", {"start": v(-21.49, 44.92) * mm, "end": v(-20.9, 44.92) * mm});
            skLineSegment(sketch, "E387", {"start": v(-20.9, 44.92) * mm, "end": v(-20.9, 46.16) * mm});
            skLineSegment(sketch, "E388", {"start": v(-20.9, 46.16) * mm, "end": v(-19.17, 46.16) * mm});
            skLineSegment(sketch, "E389", {"start": v(-19.17, 46.16) * mm, "end": v(-19.17, 44.92) * mm});
            skLineSegment(sketch, "E390", {"start": v(-19.17, 44.92) * mm, "end": v(-18.05, 44.92) * mm});
            skLineSegment(sketch, "E391", {"start": v(-18.05, 44.92) * mm, "end": v(-18.05, 43.53) * mm});
            skLineSegment(sketch, "E392", {"start": v(-18.05, 43.53) * mm, "end": v(-19.17, 43.53) * mm});
            skLineSegment(sketch, "E393", {"start": v(-19.17, 43.53) * mm, "end": v(-19.17, 40.03) * mm});
            skLineSegment(sketch, "E394", {"start": v(-19.17, 40.03) * mm, "end": v(-20.9, 40.03) * mm});
            skLineSegment(sketch, "E395", {"start": v(-20.9, 40.03) * mm, "end": v(-20.9, 41.78) * mm});
            skLineSegment(sketch, "E396", {"start": v(-17.67, 40.02) * mm, "end": v(-17.94, 40.14) * mm});
            skLineSegment(sketch, "E397", {"start": v(-17.94, 40.14) * mm, "end": v(-18.17, 40.33) * mm});
            skLineSegment(sketch, "E398", {"start": v(-18.17, 40.33) * mm, "end": v(-18.34, 40.56) * mm});
            skLineSegment(sketch, "E399", {"start": v(-18.34, 40.56) * mm, "end": v(-18.44, 40.84) * mm});
            skLineSegment(sketch, "E400", {"start": v(-18.44, 40.84) * mm, "end": v(-18.45, 40.97) * mm});
            skLineSegment(sketch, "E401", {"start": v(-18.45, 40.97) * mm, "end": v(-18.45, 41.13) * mm});
            skLineSegment(sketch, "E402", {"start": v(-18.45, 41.13) * mm, "end": v(-18.43, 41.27) * mm});
            skLineSegment(sketch, "E403", {"start": v(-18.43, 41.27) * mm, "end": v(-18.4, 41.4) * mm});
            skLineSegment(sketch, "E404", {"start": v(-18.4, 41.4) * mm, "end": v(-18.28, 41.62) * mm});
            skLineSegment(sketch, "E405", {"start": v(-18.28, 41.62) * mm, "end": v(-18.13, 41.8) * mm});
            skLineSegment(sketch, "E406", {"start": v(-18.13, 41.8) * mm, "end": v(-17.93, 41.96) * mm});
            skLineSegment(sketch, "E407", {"start": v(-17.93, 41.96) * mm, "end": v(-17.7, 42.06) * mm});
            skLineSegment(sketch, "E408", {"start": v(-17.7, 42.06) * mm, "end": v(-17.56, 42.09) * mm});
            skLineSegment(sketch, "E409", {"start": v(-17.56, 42.09) * mm, "end": v(-17.4, 42.1) * mm});
            skLineSegment(sketch, "E410", {"start": v(-17.4, 42.1) * mm, "end": v(-17.23, 42.09) * mm});
            skLineSegment(sketch, "E411", {"start": v(-17.23, 42.09) * mm, "end": v(-17.1, 42.06) * mm});
            skLineSegment(sketch, "E412", {"start": v(-17.1, 42.06) * mm, "end": v(-16.78, 41.9) * mm});
            skLineSegment(sketch, "E413", {"start": v(-16.78, 41.9) * mm, "end": v(-16.54, 41.67) * mm});
            skLineSegment(sketch, "E414", {"start": v(-16.54, 41.67) * mm, "end": v(-16.4, 41.38) * mm});
            skLineSegment(sketch, "E415", {"start": v(-16.4, 41.38) * mm, "end": v(-16.35, 41.07) * mm});
            skLineSegment(sketch, "E416", {"start": v(-16.4, 40.7) * mm, "end": v(-16.56, 40.4) * mm});
            skLineSegment(sketch, "E417", {"start": v(-16.56, 40.4) * mm, "end": v(-16.81, 40.16) * mm});
            skLineSegment(sketch, "E418", {"start": v(-16.81, 40.16) * mm, "end": v(-17.12, 40.02) * mm});
            skLineSegment(sketch, "E419", {"start": v(-17.12, 40.02) * mm, "end": v(-17.25, 40) * mm});
            skLineSegment(sketch, "E420", {"start": v(-17.25, 40) * mm, "end": v(-17.4, 40) * mm});
            skLineSegment(sketch, "E421", {"start": v(-17.4, 40) * mm, "end": v(-17.55, 40) * mm});
            skLineSegment(sketch, "E422", {"start": v(-17.55, 40) * mm, "end": v(-17.67, 40.02) * mm});
            skLineSegment(sketch, "E423", {"start": v(-17.67, 40.02) * mm, "end": v(-17.67, 40.02) * mm});
            skLineSegment(sketch, "E424", {"start": v(-56.34, 42.62) * mm, "end": v(-56.34, 42.37) * mm});
            skLineSegment(sketch, "E425", {"start": v(-16.35, 41.07) * mm, "end": v(-16.35, 40.88) * mm});
            skLineSegment(sketch, "E426", {"start": v(-16.35, 40.88) * mm, "end": v(-16.4, 40.7) * mm});
            skPoint(sketch, "E427.middle", {"position": v(-36.38, 42.42) * mm});
            skLineSegment(sketch, "E428", {"start": v(-34.62, 42.83) * mm, "end": v(-34.64, 42.62) * mm});
            skSolve(sketch);
        }
        {
            var Q0;
            Q0=qSketchRegion(id+"F15",true);
            extrude(context, id + "F16", {"entities" : qUnion([Q0]), "operationType" : NewBodyOperationType.ADD, "depth" : 2 * mm});
        }
        {
            var Q0;
            Q0=qCreatedBy(id+"F14.planeOp",FACE);
            cPlane(context, id + "F17", {"entities" : qUnion([Q0]), "cplaneType" : CPlaneType.OFFSET, "offset" : 7 * mm, "oppositeDirection" : true, "width" : 150 * mm, "height" : 150 * mm});
        }
        {
            var Q0;
            Q0=makeQuery(id+"F4.imprint","IMPRINT",FACE,{"disambiguationData":[TD([[makeQuery(id+"F4.imprint","IMPRINT",EDGE,{"derivedFrom":sQuery(id+"F4.wireOp",EDGE,"E15")}),1.0]])]});
            var Q1;
            Q1=sQuery(id+"F4.wireOp",EDGE,"E15");
            extrude(context, id + "F18", {"entities" : qUnion([Q0]), "operationType" : NewBodyOperationType.REMOVE, "surfaceEntities" : qUnion([Q1]), "endBound" : BoundingType.THROUGH_ALL, "depth" : 25 * mm});
        }
    });
